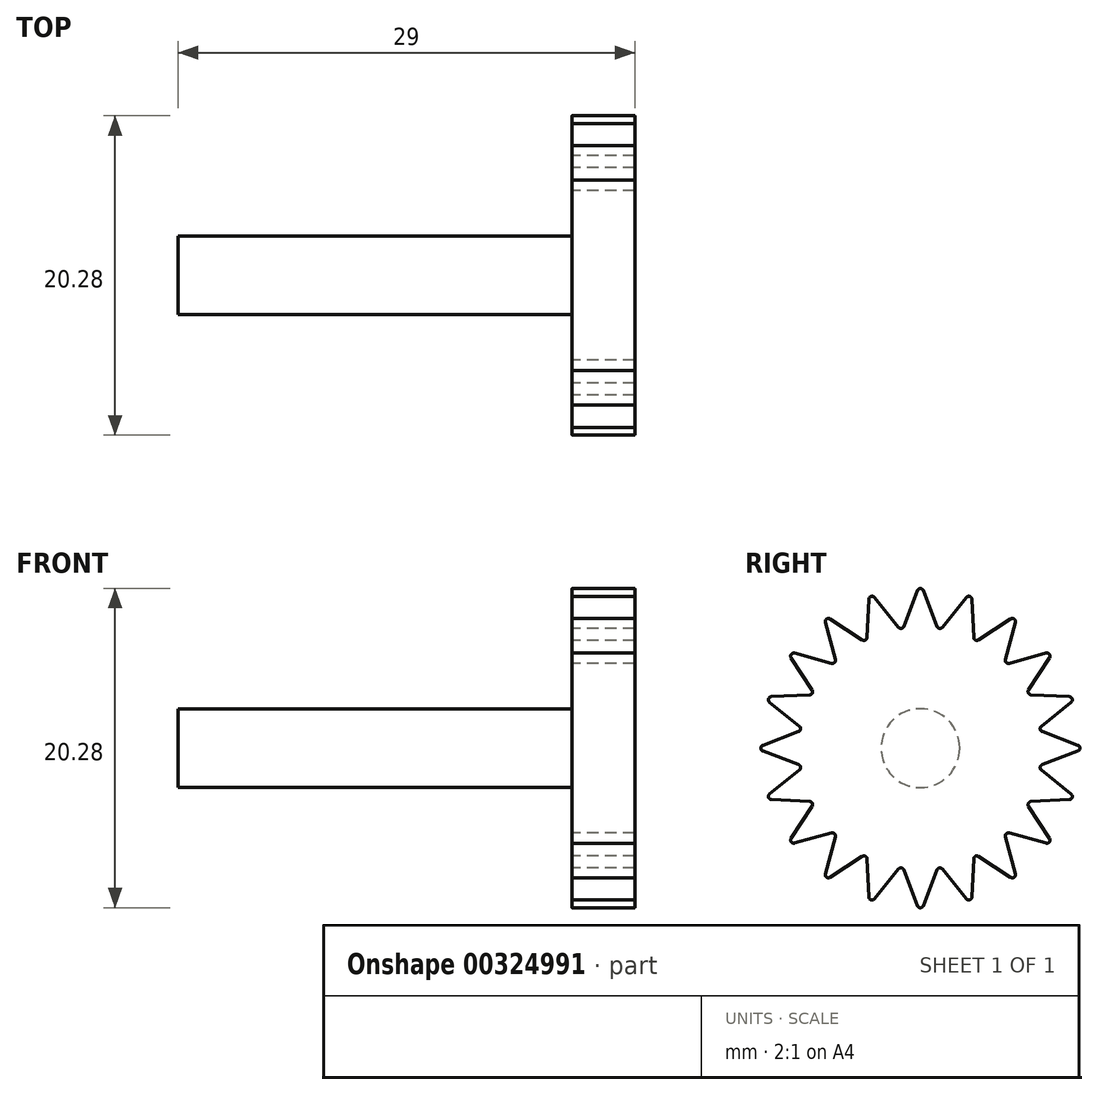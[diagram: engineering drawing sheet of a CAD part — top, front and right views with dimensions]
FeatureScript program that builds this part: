
annotation { "Feature Type Name" : "Feature", "Feature Type Description" : "" }
export const myFeature = defineFeature(function(context is Context, id is Id, definition is map)
    precondition{}
    {
        {
            var Q0;
            Q0=qCreatedBy(makeId("Right.planeOp"),FACE);
            var sketch = newSketch(context, id + "F0", { "sketchPlane" : qUnion([Q0])});
            skCircle(sketch, "E0", {"center": v(0, 0) * mm, "radius": 7.5 * mm, "construction": true});
            skLineSegment(sketch, "E1", {"start": v(-0.19, 10) * mm, "end": v(-1.05, 7.73) * mm});
            skLineSegment(sketch, "E2.MirrorCS", {"start": v(0.19, 10) * mm, "end": v(1.05, 7.73) * mm});
            skPoint(sketch, "E3.visualSharp", {"position": v(0, 10.5) * mm});
            skArc(sketch, "E3.filletArc", {"start": v(0.19, 10) * mm, "mid": v(0, 10.14) * mm, "end": v(-0.19, 10) * mm});
            skLineSegment(sketch, "E4.1.0", {"start": v(-3.27, 9.46) * mm, "end": v(-3.39, 7.03) * mm});
            skLineSegment(sketch, "E4.1.1", {"start": v(-2.91, 9.58) * mm, "end": v(-1.4, 7.68) * mm});
            skPoint(sketch, "E4.1.2", {"position": v(-3.24, 9.99) * mm});
            skArc(sketch, "E4.1.3", {"start": v(-2.91, 9.58) * mm, "mid": v(-3.13, 9.64) * mm, "end": v(-3.27, 9.46) * mm});
            skLineSegment(sketch, "E4.2.0", {"start": v(-6.03, 7.99) * mm, "end": v(-5.4, 5.64) * mm});
            skLineSegment(sketch, "E4.2.1", {"start": v(-5.73, 8.2) * mm, "end": v(-3.7, 6.87) * mm});
            skPoint(sketch, "E4.2.2", {"position": v(-6.17, 8.5) * mm});
            skArc(sketch, "E4.2.3", {"start": v(-5.73, 8.2) * mm, "mid": v(-5.96, 8.2) * mm, "end": v(-6.03, 7.99) * mm});
            skLineSegment(sketch, "E4.3.0", {"start": v(-8.2, 5.73) * mm, "end": v(-6.87, 3.7) * mm});
            skLineSegment(sketch, "E4.3.1", {"start": v(-7.99, 6.03) * mm, "end": v(-5.64, 5.4) * mm});
            skPoint(sketch, "E4.3.2", {"position": v(-8.5, 6.17) * mm});
            skArc(sketch, "E4.3.3", {"start": v(-7.99, 6.03) * mm, "mid": v(-8.2, 5.96) * mm, "end": v(-8.2, 5.73) * mm});
            skLineSegment(sketch, "E4.4.0", {"start": v(-9.58, 2.91) * mm, "end": v(-7.68, 1.4) * mm});
            skLineSegment(sketch, "E4.4.1", {"start": v(-9.46, 3.27) * mm, "end": v(-7.03, 3.39) * mm});
            skPoint(sketch, "E4.4.2", {"position": v(-9.99, 3.24) * mm});
            skArc(sketch, "E4.4.3", {"start": v(-9.46, 3.27) * mm, "mid": v(-9.64, 3.13) * mm, "end": v(-9.58, 2.91) * mm});
            skLineSegment(sketch, "E4.5.0", {"start": v(-10, -0.19) * mm, "end": v(-7.73, -1.05) * mm});
            skLineSegment(sketch, "E4.5.1", {"start": v(-10, 0.19) * mm, "end": v(-7.73, 1.05) * mm});
            skPoint(sketch, "E4.5.2", {"position": v(-10.5, 0) * mm});
            skArc(sketch, "E4.5.3", {"start": v(-10, 0.19) * mm, "mid": v(-10.14, 0) * mm, "end": v(-10, -0.19) * mm});
            skLineSegment(sketch, "E4.6.0", {"start": v(-9.46, -3.27) * mm, "end": v(-7.03, -3.39) * mm});
            skLineSegment(sketch, "E4.6.1", {"start": v(-9.58, -2.91) * mm, "end": v(-7.68, -1.4) * mm});
            skPoint(sketch, "E4.6.2", {"position": v(-9.99, -3.24) * mm});
            skArc(sketch, "E4.6.3", {"start": v(-9.58, -2.91) * mm, "mid": v(-9.64, -3.13) * mm, "end": v(-9.46, -3.27) * mm});
            skLineSegment(sketch, "E4.7.0", {"start": v(-7.99, -6.03) * mm, "end": v(-5.64, -5.4) * mm});
            skLineSegment(sketch, "E4.7.1", {"start": v(-8.2, -5.73) * mm, "end": v(-6.87, -3.7) * mm});
            skPoint(sketch, "E4.7.2", {"position": v(-8.5, -6.17) * mm});
            skArc(sketch, "E4.7.3", {"start": v(-8.2, -5.73) * mm, "mid": v(-8.2, -5.96) * mm, "end": v(-7.99, -6.03) * mm});
            skLineSegment(sketch, "E4.8.0", {"start": v(-5.73, -8.2) * mm, "end": v(-3.7, -6.87) * mm});
            skLineSegment(sketch, "E4.8.1", {"start": v(-6.03, -7.99) * mm, "end": v(-5.4, -5.64) * mm});
            skPoint(sketch, "E4.8.2", {"position": v(-6.17, -8.5) * mm});
            skArc(sketch, "E4.8.3", {"start": v(-6.03, -7.99) * mm, "mid": v(-5.96, -8.2) * mm, "end": v(-5.73, -8.2) * mm});
            skLineSegment(sketch, "E4.9.0", {"start": v(-2.91, -9.58) * mm, "end": v(-1.4, -7.68) * mm});
            skLineSegment(sketch, "E4.9.1", {"start": v(-3.27, -9.46) * mm, "end": v(-3.39, -7.03) * mm});
            skPoint(sketch, "E4.9.2", {"position": v(-3.24, -9.99) * mm});
            skArc(sketch, "E4.9.3", {"start": v(-3.27, -9.46) * mm, "mid": v(-3.13, -9.64) * mm, "end": v(-2.91, -9.58) * mm});
            skLineSegment(sketch, "E4.10.0", {"start": v(0.19, -10) * mm, "end": v(1.05, -7.73) * mm});
            skLineSegment(sketch, "E4.10.1", {"start": v(-0.19, -10) * mm, "end": v(-1.05, -7.73) * mm});
            skPoint(sketch, "E4.10.2", {"position": v(0, -10.5) * mm});
            skArc(sketch, "E4.10.3", {"start": v(-0.19, -10) * mm, "mid": v(0, -10.14) * mm, "end": v(0.19, -10) * mm});
            skLineSegment(sketch, "E4.11.0", {"start": v(3.27, -9.46) * mm, "end": v(3.39, -7.03) * mm});
            skLineSegment(sketch, "E4.11.1", {"start": v(2.91, -9.58) * mm, "end": v(1.4, -7.68) * mm});
            skPoint(sketch, "E4.11.2", {"position": v(3.24, -9.99) * mm});
            skArc(sketch, "E4.11.3", {"start": v(2.91, -9.58) * mm, "mid": v(3.13, -9.64) * mm, "end": v(3.27, -9.46) * mm});
            skLineSegment(sketch, "E4.12.0", {"start": v(6.03, -7.99) * mm, "end": v(5.4, -5.64) * mm});
            skLineSegment(sketch, "E4.12.1", {"start": v(5.73, -8.2) * mm, "end": v(3.7, -6.87) * mm});
            skPoint(sketch, "E4.12.2", {"position": v(6.17, -8.5) * mm});
            skArc(sketch, "E4.12.3", {"start": v(5.73, -8.2) * mm, "mid": v(5.96, -8.2) * mm, "end": v(6.03, -7.99) * mm});
            skLineSegment(sketch, "E4.13.0", {"start": v(8.2, -5.73) * mm, "end": v(6.87, -3.7) * mm});
            skLineSegment(sketch, "E4.13.1", {"start": v(7.99, -6.03) * mm, "end": v(5.64, -5.4) * mm});
            skPoint(sketch, "E4.13.2", {"position": v(8.5, -6.17) * mm});
            skArc(sketch, "E4.13.3", {"start": v(7.99, -6.03) * mm, "mid": v(8.2, -5.96) * mm, "end": v(8.2, -5.73) * mm});
            skLineSegment(sketch, "E4.14.0", {"start": v(9.58, -2.91) * mm, "end": v(7.68, -1.4) * mm});
            skLineSegment(sketch, "E4.14.1", {"start": v(9.46, -3.27) * mm, "end": v(7.03, -3.39) * mm});
            skPoint(sketch, "E4.14.2", {"position": v(9.99, -3.24) * mm});
            skArc(sketch, "E4.14.3", {"start": v(9.46, -3.27) * mm, "mid": v(9.64, -3.13) * mm, "end": v(9.58, -2.91) * mm});
            skLineSegment(sketch, "E4.15.0", {"start": v(10, 0.19) * mm, "end": v(7.73, 1.05) * mm});
            skLineSegment(sketch, "E4.15.1", {"start": v(10, -0.19) * mm, "end": v(7.73, -1.05) * mm});
            skPoint(sketch, "E4.15.2", {"position": v(10.5, 0) * mm});
            skArc(sketch, "E4.15.3", {"start": v(10, -0.19) * mm, "mid": v(10.14, 0) * mm, "end": v(10, 0.19) * mm});
            skLineSegment(sketch, "E4.16.0", {"start": v(9.46, 3.27) * mm, "end": v(7.03, 3.39) * mm});
            skLineSegment(sketch, "E4.16.1", {"start": v(9.58, 2.91) * mm, "end": v(7.68, 1.4) * mm});
            skPoint(sketch, "E4.16.2", {"position": v(9.99, 3.24) * mm});
            skArc(sketch, "E4.16.3", {"start": v(9.58, 2.91) * mm, "mid": v(9.64, 3.13) * mm, "end": v(9.46, 3.27) * mm});
            skLineSegment(sketch, "E4.17.0", {"start": v(7.99, 6.03) * mm, "end": v(5.64, 5.4) * mm});
            skLineSegment(sketch, "E4.17.1", {"start": v(8.2, 5.73) * mm, "end": v(6.87, 3.7) * mm});
            skPoint(sketch, "E4.17.2", {"position": v(8.5, 6.17) * mm});
            skArc(sketch, "E4.17.3", {"start": v(8.2, 5.73) * mm, "mid": v(8.2, 5.96) * mm, "end": v(7.99, 6.03) * mm});
            skLineSegment(sketch, "E4.18.0", {"start": v(5.73, 8.2) * mm, "end": v(3.7, 6.87) * mm});
            skLineSegment(sketch, "E4.18.1", {"start": v(6.03, 7.99) * mm, "end": v(5.4, 5.64) * mm});
            skPoint(sketch, "E4.18.2", {"position": v(6.17, 8.5) * mm});
            skArc(sketch, "E4.18.3", {"start": v(6.03, 7.99) * mm, "mid": v(5.96, 8.2) * mm, "end": v(5.73, 8.2) * mm});
            skLineSegment(sketch, "E4.19.0", {"start": v(2.91, 9.58) * mm, "end": v(1.4, 7.68) * mm});
            skLineSegment(sketch, "E4.19.1", {"start": v(3.27, 9.46) * mm, "end": v(3.39, 7.03) * mm});
            skPoint(sketch, "E4.19.2", {"position": v(3.24, 9.99) * mm});
            skArc(sketch, "E4.19.3", {"start": v(3.27, 9.46) * mm, "mid": v(3.13, 9.64) * mm, "end": v(2.91, 9.58) * mm});
            skPoint(sketch, "E5.visualSharp", {"position": v(1.17, 7.4) * mm});
            skArc(sketch, "E5.filletArc", {"start": v(1.05, 7.73) * mm, "mid": v(1.2, 7.6) * mm, "end": v(1.4, 7.68) * mm});
            skPoint(sketch, "E6.visualSharp", {"position": v(3.4, 6.68) * mm});
            skArc(sketch, "E6.filletArc", {"start": v(3.39, 7.03) * mm, "mid": v(3.5, 6.86) * mm, "end": v(3.7, 6.87) * mm});
            skPoint(sketch, "E7.visualSharp", {"position": v(5.3, 5.3) * mm});
            skArc(sketch, "E7.filletArc", {"start": v(5.4, 5.64) * mm, "mid": v(5.45, 5.45) * mm, "end": v(5.64, 5.4) * mm});
            skPoint(sketch, "E8.visualSharp", {"position": v(6.68, 3.4) * mm});
            skArc(sketch, "E8.filletArc", {"start": v(6.87, 3.7) * mm, "mid": v(6.86, 3.5) * mm, "end": v(7.03, 3.39) * mm});
            skPoint(sketch, "E9.visualSharp", {"position": v(7.4, 1.17) * mm});
            skArc(sketch, "E9.filletArc", {"start": v(7.68, 1.4) * mm, "mid": v(7.6, 1.2) * mm, "end": v(7.73, 1.05) * mm});
            skPoint(sketch, "E10.visualSharp", {"position": v(7.4, -1.17) * mm});
            skArc(sketch, "E10.filletArc", {"start": v(7.73, -1.05) * mm, "mid": v(7.6, -1.2) * mm, "end": v(7.68, -1.4) * mm});
            skPoint(sketch, "E11.visualSharp", {"position": v(-1.17, 7.4) * mm});
            skArc(sketch, "E11.filletArc", {"start": v(-1.4, 7.68) * mm, "mid": v(-1.2, 7.6) * mm, "end": v(-1.05, 7.73) * mm});
            skPoint(sketch, "E12.visualSharp", {"position": v(-3.4, 6.68) * mm});
            skArc(sketch, "E12.filletArc", {"start": v(-3.7, 6.87) * mm, "mid": v(-3.5, 6.86) * mm, "end": v(-3.39, 7.03) * mm});
            skPoint(sketch, "E13.visualSharp", {"position": v(-5.3, 5.3) * mm});
            skArc(sketch, "E13.filletArc", {"start": v(-5.64, 5.4) * mm, "mid": v(-5.45, 5.45) * mm, "end": v(-5.4, 5.64) * mm});
            skPoint(sketch, "E14.visualSharp", {"position": v(-6.68, 3.4) * mm});
            skArc(sketch, "E14.filletArc", {"start": v(-7.03, 3.39) * mm, "mid": v(-6.86, 3.5) * mm, "end": v(-6.87, 3.7) * mm});
            skPoint(sketch, "E15.visualSharp", {"position": v(-7.4, 1.17) * mm});
            skArc(sketch, "E15.filletArc", {"start": v(-7.73, 1.05) * mm, "mid": v(-7.6, 1.2) * mm, "end": v(-7.68, 1.4) * mm});
            skPoint(sketch, "E16.visualSharp", {"position": v(-7.4, -1.17) * mm});
            skArc(sketch, "E16.filletArc", {"start": v(-7.68, -1.4) * mm, "mid": v(-7.6, -1.2) * mm, "end": v(-7.73, -1.05) * mm});
            skPoint(sketch, "E17.visualSharp", {"position": v(-6.68, -3.4) * mm});
            skArc(sketch, "E17.filletArc", {"start": v(-6.87, -3.7) * mm, "mid": v(-6.86, -3.5) * mm, "end": v(-7.03, -3.39) * mm});
            skPoint(sketch, "E18.visualSharp", {"position": v(-5.3, -5.3) * mm});
            skArc(sketch, "E18.filletArc", {"start": v(-5.4, -5.64) * mm, "mid": v(-5.45, -5.45) * mm, "end": v(-5.64, -5.4) * mm});
            skPoint(sketch, "E19.visualSharp", {"position": v(-3.4, -6.68) * mm});
            skArc(sketch, "E19.filletArc", {"start": v(-3.39, -7.03) * mm, "mid": v(-3.5, -6.86) * mm, "end": v(-3.7, -6.87) * mm});
            skPoint(sketch, "E20.visualSharp", {"position": v(-1.17, -7.4) * mm});
            skArc(sketch, "E20.filletArc", {"start": v(-1.05, -7.73) * mm, "mid": v(-1.2, -7.6) * mm, "end": v(-1.4, -7.68) * mm});
            skPoint(sketch, "E21.visualSharp", {"position": v(1.17, -7.4) * mm});
            skArc(sketch, "E21.filletArc", {"start": v(1.4, -7.68) * mm, "mid": v(1.2, -7.6) * mm, "end": v(1.05, -7.73) * mm});
            skPoint(sketch, "E22.visualSharp", {"position": v(3.4, -6.68) * mm});
            skArc(sketch, "E22.filletArc", {"start": v(3.7, -6.87) * mm, "mid": v(3.5, -6.86) * mm, "end": v(3.39, -7.03) * mm});
            skPoint(sketch, "E23.visualSharp", {"position": v(5.3, -5.3) * mm});
            skArc(sketch, "E23.filletArc", {"start": v(5.64, -5.4) * mm, "mid": v(5.45, -5.45) * mm, "end": v(5.4, -5.64) * mm});
            skPoint(sketch, "E24.visualSharp", {"position": v(6.68, -3.4) * mm});
            skArc(sketch, "E24.filletArc", {"start": v(7.03, -3.39) * mm, "mid": v(6.86, -3.5) * mm, "end": v(6.87, -3.7) * mm});
            skSolve(sketch);
        }
        {
            var Q0;
            Q0=makeQuery(id+"F0.imprint","IMPRINT",FACE,{"disambiguationData":[TD([[makeQuery(id+"F0.imprint","IMPRINT",EDGE,{"derivedFrom":sQuery(id+"F0.wireOp",EDGE,"E1")}),1.0]])]});
            extrude(context, id + "F1", {"entities" : qUnion([Q0]), "depth" : 4 * mm});
        }
        {
            var Q0;
            Q0=qCreatedBy(makeId("Right.planeOp"),FACE);
            var sketch = newSketch(context, id + "F2", { "sketchPlane" : qUnion([Q0])});
            skCircle(sketch, "E25", {"center": v(0, 0) * mm, "radius": 2.5 * mm});
            skSolve(sketch);
        }
        {
            var Q0;
            Q0=qSketchRegion(id+"F2",true);
            extrude(context, id + "F3", {"entities" : qUnion([Q0]), "operationType" : NewBodyOperationType.ADD, "oppositeDirection" : true, "depth" : 25 * mm});
        }
    });
